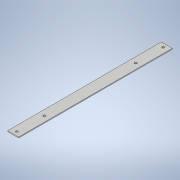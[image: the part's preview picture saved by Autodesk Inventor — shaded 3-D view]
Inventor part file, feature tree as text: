
AUTODESK INVENTOR PART (.ipt)
format: ipt  version: 2021 (Build 250183000, 183)  size: 113,664 bytes
history: native  units: in
note: dims shown in document units (in); Inventor stores cm internally (conversion verified against a paired STEP export)
features: extrude x2, sketch x2
ambient origin geometry x8: Origin, YZ Plane, XZ Plane, XY Plane, X Axis, Y Axis, Z Axis, Center Point
bodies: Solid1 (feature_tree)
feature tree (4):
  extrude  "Extrusion1"  Depth=21.0in
  extrude  "Extrusion2"  Depth=0.125in
  sketch  "Sketch1"  dims[d0=1.5in d1=21.0in]
  sketch  "Sketch2"  dims[d2=0.125in d3=0.0in d5=0.3125in d7=0.3125in d10=0.3125in d11=0.3125in d12=1.0in d13=0.0in d14=0.5in d15=4.25in d16=0.5in d17=4.25in]
